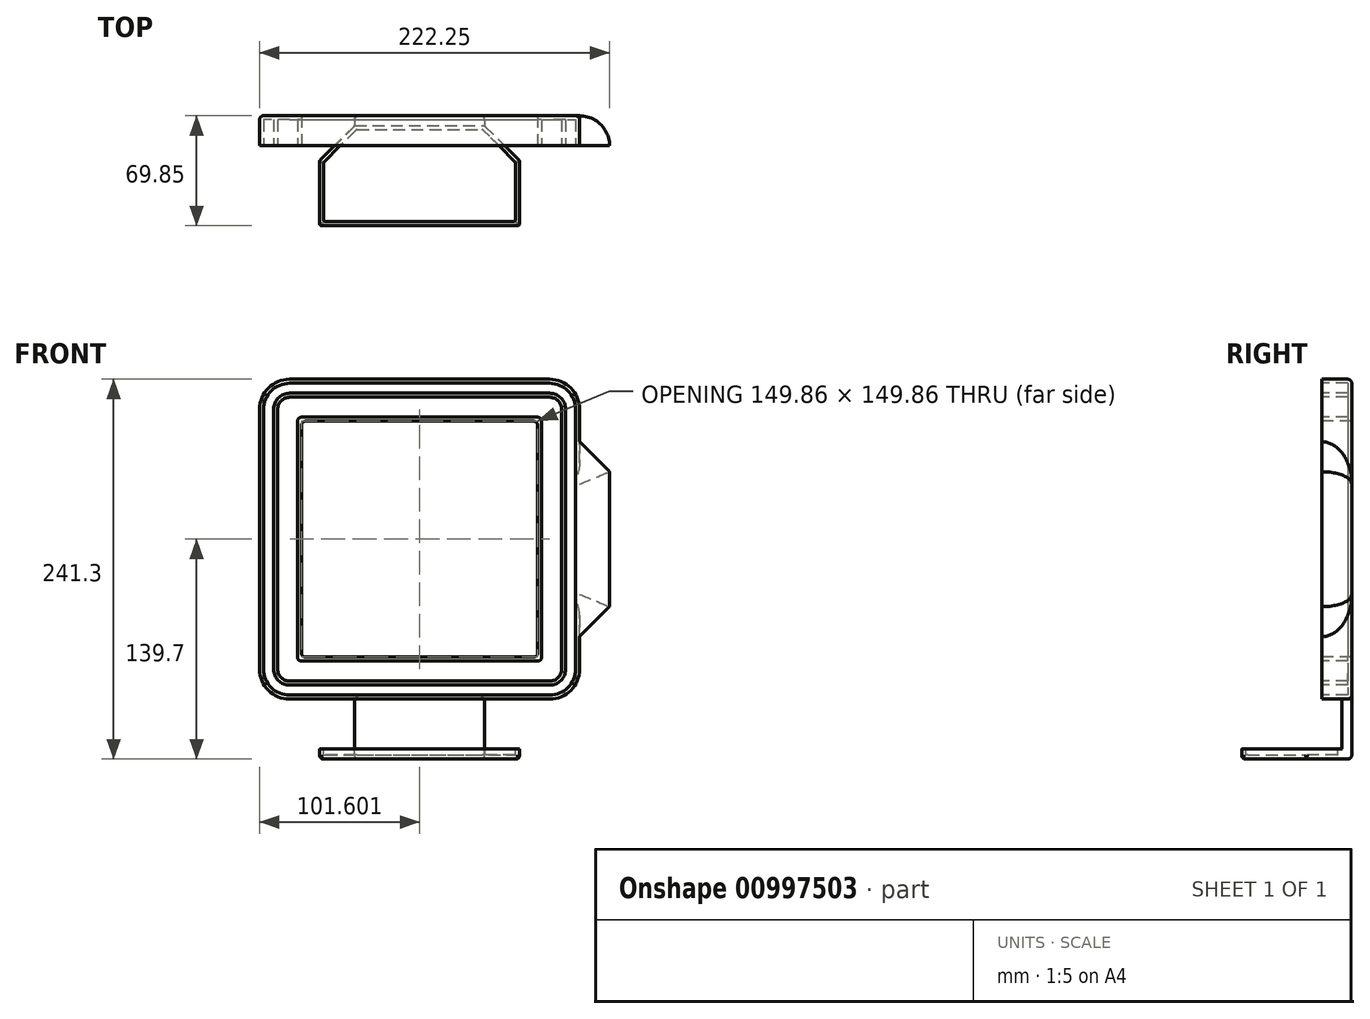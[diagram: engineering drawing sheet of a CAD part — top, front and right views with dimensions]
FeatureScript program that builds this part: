
annotation { "Feature Type Name" : "Feature", "Feature Type Description" : "" }
export const myFeature = defineFeature(function(context is Context, id is Id, definition is map)
    precondition{}
    {
        {
            var Q0;
            Q0=qCreatedBy(makeId("Front.planeOp"),FACE);
            var sketch = newSketch(context, id + "F0", { "sketchPlane" : qUnion([Q0])});
            skLineSegment(sketch, "E0.bottom", {"start": v(-101.6, 108.1) * mm, "end": v(101.6, 108.1) * mm});
            skLineSegment(sketch, "E0.top", {"start": v(-101.6, -95.1) * mm, "end": v(101.6, -95.1) * mm});
            skLineSegment(sketch, "E0.left", {"start": v(-101.6, 108.1) * mm, "end": v(-101.6, -95.1) * mm});
            skLineSegment(sketch, "E0.right", {"start": v(101.6, 108.1) * mm, "end": v(101.6, -95.1) * mm});
            skSolve(sketch);
        }
        {
            var Q0;
            Q0=makeQuery(id+"F0.imprint","IMPRINT",FACE,{"disambiguationData":[TD([[makeQuery(id+"F0.imprint","IMPRINT",EDGE,{"derivedFrom":sQuery(id+"F0.wireOp",EDGE,"E0.bottom")}),-1.0]])]});
            extrude(context, id + "F1", {"entities" : qUnion([Q0]), "depth" : 19.05 * mm, "offsetDistance" : 25.4 * mm});
        }
        {
            var Q0;
            Q0=makeQuery(id+"F1.opExtrude","SWEPT_EDGE",EDGE,{"disambiguationData":[OSD([sQuery(id+"F0.wireOp",EDGE,"E0.bottom"),sQuery(id+"F0.wireOp",EDGE,"E0.left")])]});
            var Q1;
            Q1=makeQuery(id+"F1.opExtrude","SWEPT_EDGE",EDGE,{"disambiguationData":[OSD([sQuery(id+"F0.wireOp",EDGE,"E0.top"),sQuery(id+"F0.wireOp",EDGE,"E0.left")])]});
            var Q2;
            Q2=makeQuery(id+"F1.opExtrude","SWEPT_EDGE",EDGE,{"disambiguationData":[OSD([sQuery(id+"F0.wireOp",EDGE,"E0.top"),sQuery(id+"F0.wireOp",EDGE,"E0.right")])]});
            var Q3;
            Q3=makeQuery(id+"F1.opExtrude","SWEPT_EDGE",EDGE,{"disambiguationData":[OSD([sQuery(id+"F0.wireOp",EDGE,"E0.bottom"),sQuery(id+"F0.wireOp",EDGE,"E0.right")])]});
            fillet(context, id + "F2", {"entities" : qUnion([Q0, Q1, Q2, Q3]), "tangentPropagation" : true, "radius" : 19.05 * mm, "defaultsChanged" : false, "vertexSettings" : [], "allowEdgeOverflow" : false});
        }
        {
            var Q0;
            Q0=makeQuery(id+"F1.opExtrude","CAP_FACE",FACE,{"disambiguationData":[OSD([sQuery(id+"F0.wireOp",EDGE,"E0.bottom"),sQuery(id+"F0.wireOp",EDGE,"E0.top"),sQuery(id+"F0.wireOp",EDGE,"E0.left"),sQuery(id+"F0.wireOp",EDGE,"E0.right")])],"isStart":false});
            var sketch = newSketch(context, id + "F3", { "sketchPlane" : qUnion([Q0])});
            skLineSegment(sketch, "E1.0", {"start": v(-82.55, 99.21) * mm, "end": v(82.55, 99.21) * mm});
            skArc(sketch, "E1.1", {"start": v(92.71, 89.05) * mm, "mid": v(89.74, 96.23) * mm, "end": v(82.55, 99.21) * mm});
            skArc(sketch, "E1.2", {"start": v(-82.55, 99.21) * mm, "mid": v(-89.73, 96.23) * mm, "end": v(-92.7, 89.05) * mm});
            skLineSegment(sketch, "E1.3", {"start": v(92.71, 89.05) * mm, "end": v(92.71, -76.05) * mm});
            skLineSegment(sketch, "E1.4", {"start": v(-92.7, 89.05) * mm, "end": v(-92.7, -76.05) * mm});
            skArc(sketch, "E1.5", {"start": v(-92.7, -76.05) * mm, "mid": v(-89.73, -83.23) * mm, "end": v(-82.55, -86.2) * mm});
            skLineSegment(sketch, "E1.6", {"start": v(-82.55, -86.2) * mm, "end": v(82.55, -86.2) * mm});
            skArc(sketch, "E1.7", {"start": v(82.55, -86.2) * mm, "mid": v(89.74, -83.23) * mm, "end": v(92.71, -76.05) * mm});
            skLineSegment(sketch, "E2.0", {"start": v(-74.93, 81.43) * mm, "end": v(-74.93, -68.43) * mm});
            skLineSegment(sketch, "E2.1", {"start": v(-74.93, 81.43) * mm, "end": v(74.93, 81.43) * mm});
            skLineSegment(sketch, "E2.2", {"start": v(74.93, 81.43) * mm, "end": v(74.93, -68.43) * mm});
            skLineSegment(sketch, "E2.3", {"start": v(-74.93, -68.43) * mm, "end": v(74.93, -68.43) * mm});
            skArc(sketch, "E3.0", {"start": v(-82.55, 96.67) * mm, "mid": v(-87.94, 94.44) * mm, "end": v(-90.17, 89.05) * mm});
            skLineSegment(sketch, "E3.1", {"start": v(-82.55, 96.67) * mm, "end": v(82.55, 96.67) * mm});
            skLineSegment(sketch, "E3.2", {"start": v(-90.17, 89.05) * mm, "end": v(-90.17, -76.05) * mm});
            skArc(sketch, "E3.3", {"start": v(90.17, 89.05) * mm, "mid": v(87.94, 94.44) * mm, "end": v(82.55, 96.67) * mm});
            skArc(sketch, "E3.4", {"start": v(-90.17, -76.05) * mm, "mid": v(-87.94, -81.44) * mm, "end": v(-82.55, -83.67) * mm});
            skLineSegment(sketch, "E3.5", {"start": v(-82.55, -83.67) * mm, "end": v(82.55, -83.67) * mm});
            skArc(sketch, "E3.6", {"start": v(82.55, -83.67) * mm, "mid": v(87.94, -81.44) * mm, "end": v(90.17, -76.05) * mm});
            skLineSegment(sketch, "E3.7", {"start": v(90.17, 89.05) * mm, "end": v(90.17, -76.05) * mm});
            skLineSegment(sketch, "E4.0", {"start": v(-77.47, 83.97) * mm, "end": v(-77.47, -70.97) * mm});
            skLineSegment(sketch, "E4.1", {"start": v(-77.47, 83.97) * mm, "end": v(77.47, 83.97) * mm});
            skLineSegment(sketch, "E4.2", {"start": v(77.47, 83.97) * mm, "end": v(77.47, -70.97) * mm});
            skLineSegment(sketch, "E4.3", {"start": v(-77.47, -70.97) * mm, "end": v(77.47, -70.97) * mm});
            skArc(sketch, "E5.0", {"start": v(-82.55, 105.56) * mm, "mid": v(-94.22, 100.72) * mm, "end": v(-99.06, 89.05) * mm});
            skLineSegment(sketch, "E5.1", {"start": v(-82.55, 105.56) * mm, "end": v(82.55, 105.56) * mm});
            skLineSegment(sketch, "E5.2", {"start": v(-99.06, 89.05) * mm, "end": v(-99.06, -76.05) * mm});
            skArc(sketch, "E5.3", {"start": v(99.06, 89.05) * mm, "mid": v(94.23, 100.72) * mm, "end": v(82.55, 105.56) * mm});
            skArc(sketch, "E5.4", {"start": v(-99.06, -76.05) * mm, "mid": v(-94.22, -87.72) * mm, "end": v(-82.55, -92.56) * mm});
            skLineSegment(sketch, "E5.5", {"start": v(-82.55, -92.56) * mm, "end": v(82.55, -92.56) * mm});
            skArc(sketch, "E5.6", {"start": v(82.55, -92.56) * mm, "mid": v(94.23, -87.72) * mm, "end": v(99.06, -76.05) * mm});
            skLineSegment(sketch, "E5.7", {"start": v(99.06, 89.05) * mm, "end": v(99.06, -76.05) * mm});
            skSolve(sketch);
        }
        {
            var Q0;
            Q0=makeQuery(id+"F3.imprint","IMPRINT",FACE,{"disambiguationData":[TD([[makeQuery(id+"F3.imprint","IMPRINT",EDGE,{"derivedFrom":sQuery(id+"F3.wireOp",EDGE,"E2.0")}),1.0]])]});
            extrude(context, id + "F4", {"entities" : qUnion([Q0]), "operationType" : NewBodyOperationType.REMOVE, "oppositeDirection" : true, "depth" : 25.4 * mm, "offsetDistance" : 25.4 * mm, "hasSecondDirection" : true, "secondDirectionOppositeDirection" : false, "secondDirectionDepth" : 25.4 * mm});
        }
        {
            var Q0;
            Q0=makeQuery(id+"F3.imprint","IMPRINT",FACE,{"disambiguationData":[TD([[makeQuery(id+"F3.imprint","IMPRINT",EDGE,{"derivedFrom":sQuery(id+"F3.wireOp",EDGE,"E3.0")}),1.0]])]});
            var Q1;
            Q1=makeQuery(id+"F3.imprint","IMPRINT",FACE,{"disambiguationData":[TD([[makeQuery(id+"F3.imprint","IMPRINT",EDGE,{"derivedFrom":sQuery(id+"F3.wireOp",EDGE,"E1.0")}),1.0]])]});
            extrude(context, id + "F5", {"entities" : qUnion([Q0, Q1]), "operationType" : NewBodyOperationType.REMOVE, "oppositeDirection" : true, "depth" : 16.5 * mm, "offsetDistance" : 25.4 * mm});
        }
        {
            var Q0;
            Q0=makeQuery(id+"F4.boolean.opBoolean","COPY",EDGE,{"derivedFrom":makeQuery(id+"F4.opExtrude","SWEPT_EDGE",EDGE,{"disambiguationData":[OSD([sQuery(id+"F3.wireOp",EDGE,"E2.1"),sQuery(id+"F3.wireOp",EDGE,"E2.2")])]})});
            var Q1;
            Q1=makeQuery(id+"F5.boolean.opBoolean","COPY",EDGE,{"derivedFrom":makeQuery(id+"F5.opExtrude","SWEPT_EDGE",EDGE,{"disambiguationData":[OSD([sQuery(id+"F3.wireOp",EDGE,"E4.1"),sQuery(id+"F3.wireOp",EDGE,"E4.2")])]})});
            var Q2;
            Q2=makeQuery(id+"F4.boolean.opBoolean","COPY",EDGE,{"derivedFrom":makeQuery(id+"F4.opExtrude","SWEPT_EDGE",EDGE,{"disambiguationData":[OSD([sQuery(id+"F3.wireOp",EDGE,"E2.2"),sQuery(id+"F3.wireOp",EDGE,"E2.3")])]})});
            var Q3;
            Q3=makeQuery(id+"F5.boolean.opBoolean","COPY",EDGE,{"derivedFrom":makeQuery(id+"F5.opExtrude","SWEPT_EDGE",EDGE,{"disambiguationData":[OSD([sQuery(id+"F3.wireOp",EDGE,"E4.2"),sQuery(id+"F3.wireOp",EDGE,"E4.3")])]})});
            var Q4;
            Q4=makeQuery(id+"F5.boolean.opBoolean","COPY",EDGE,{"derivedFrom":makeQuery(id+"F5.opExtrude","SWEPT_EDGE",EDGE,{"disambiguationData":[OSD([sQuery(id+"F3.wireOp",EDGE,"E4.0"),sQuery(id+"F3.wireOp",EDGE,"E4.3")])]})});
            var Q5;
            Q5=makeQuery(id+"F4.boolean.opBoolean","COPY",EDGE,{"derivedFrom":makeQuery(id+"F4.opExtrude","SWEPT_EDGE",EDGE,{"disambiguationData":[OSD([sQuery(id+"F3.wireOp",EDGE,"E2.0"),sQuery(id+"F3.wireOp",EDGE,"E2.3")])]})});
            var Q6;
            Q6=makeQuery(id+"F4.boolean.opBoolean","COPY",EDGE,{"derivedFrom":makeQuery(id+"F4.opExtrude","SWEPT_EDGE",EDGE,{"disambiguationData":[OSD([sQuery(id+"F3.wireOp",EDGE,"E2.0"),sQuery(id+"F3.wireOp",EDGE,"E2.1")])]})});
            var Q7;
            Q7=makeQuery(id+"F5.boolean.opBoolean","COPY",EDGE,{"derivedFrom":makeQuery(id+"F5.opExtrude","SWEPT_EDGE",EDGE,{"disambiguationData":[OSD([sQuery(id+"F3.wireOp",EDGE,"E4.0"),sQuery(id+"F3.wireOp",EDGE,"E4.1")])]})});
            fillet(context, id + "F6", {"entities" : qUnion([Q0, Q1, Q2, Q3, Q4, Q5, Q6, Q7]), "tangentPropagation" : true, "radius" : 2.54 * mm, "defaultsChanged" : true, "vertexSettings" : [], "allowEdgeOverflow" : false});
        }
        {
            var Q0;
            {var subQ0=sQuery(id+"F0.wireOp",EDGE,"E0.right");var subQ1=sQuery(id+"F0.wireOp",EDGE,"E0.top");var subQ2=sQuery(id+"F0.wireOp",EDGE,"E0.left");var subQ3=sQuery(id+"F0.wireOp",EDGE,"E0.bottom");Q0=makeQuery(id+"F5.boolean.opBoolean","SPLIT",FACE,{"disambiguationData":[TD([makeQuery(id+"F1.opExtrude","SWEPT_FACE",FACE,{"disambiguationData":[OSD([subQ3])]})])],"derivedFrom":makeQuery(id+"F1.opExtrude","CAP_FACE",FACE,{"disambiguationData":[OSD([subQ3,subQ1,subQ2,subQ0])],"isStart":false})});}
            var sketch = newSketch(context, id + "F7", { "sketchPlane" : qUnion([Q0])});
            skPoint(sketch, "E6", {"position": v(0, -95.1) * mm});
            skPoint(sketch, "E7", {"position": v(-41.27, -95.1) * mm});
            skPoint(sketch, "E8", {"position": v(41.28, -95.1) * mm});
            skPoint(sketch, "E9", {"position": v(82.55, -95.1) * mm});
            skPoint(sketch, "E10", {"position": v(-82.55, -95.1) * mm});
            skPoint(sketch, "E11", {"position": v(101.6, 89.05) * mm});
            skPoint(sketch, "E12", {"position": v(101.6, 6.5) * mm});
            skPoint(sketch, "E13", {"position": v(101.6, -76.05) * mm});
            skPoint(sketch, "E14", {"position": v(101.6, -34.77) * mm});
            skPoint(sketch, "E15", {"position": v(101.6, 47.78) * mm});
            skPoint(sketch, "E16", {"position": v(101.6, 68.41) * mm});
            skPoint(sketch, "E17", {"position": v(101.6, -55.41) * mm});
            skLineSegment(sketch, "E18.bottom", {"start": v(101.6, 68.41) * mm, "end": v(120.65, 68.41) * mm});
            skLineSegment(sketch, "E18.top", {"start": v(101.6, -55.41) * mm, "end": v(120.65, -55.41) * mm});
            skLineSegment(sketch, "E18.left", {"start": v(101.6, 68.41) * mm, "end": v(101.6, -55.41) * mm});
            skLineSegment(sketch, "E18.right", {"start": v(120.65, 68.41) * mm, "end": v(120.65, -55.41) * mm});
            skSolve(sketch);
        }
        {
            var Q0;
            Q0=makeQuery(id+"F7.imprint","IMPRINT",FACE,{"disambiguationData":[TD([[makeQuery(id+"F7.imprint","IMPRINT",EDGE,{"derivedFrom":sQuery(id+"F7.wireOp",EDGE,"E18.bottom")}),-1.0]])]});
            extrude(context, id + "F8", {"entities" : qUnion([Q0]), "operationType" : NewBodyOperationType.ADD, "oppositeDirection" : true, "depth" : 19.05 * mm, "offsetDistance" : 25.4 * mm});
        }
        {
            var Q0;
            Q0=makeQuery(id+"F8.opExtrude","SWEPT_EDGE",EDGE,{"disambiguationData":[OSD([sQuery(id+"F7.wireOp",EDGE,"E18.top"),sQuery(id+"F7.wireOp",EDGE,"E18.right")])]});
            var Q1;
            Q1=makeQuery(id+"F8.opExtrude","SWEPT_EDGE",EDGE,{"disambiguationData":[OSD([sQuery(id+"F7.wireOp",EDGE,"E18.bottom"),sQuery(id+"F7.wireOp",EDGE,"E18.right")])]});
            chamfer(context, id + "F9", {"entities" : qUnion([Q0, Q1]), "width" : 19.05 * mm, "tangentPropagation" : true});
        }
        {
            var Q0;
            Q0=makeQuery(id+"F8.opExtrude","CAP_EDGE",EDGE,{"disambiguationData":[OSD([sQuery(id+"F7.wireOp",EDGE,"E18.right")])],"isStart":false});
            var Q1;
            {var subQ0=sQuery(id+"F7.wireOp",EDGE,"E18.right");var subQ1=sQuery(id+"F7.wireOp",EDGE,"E18.top");Q1=makeQuery(id+"F9.opChamfer","BLEND_EDGE",EDGE,{"blendedFrom":[makeQuery(id+"F8.opExtrude","SWEPT_EDGE",EDGE,{"disambiguationData":[OSD([subQ1,subQ0])]}),makeQuery(id+"F8.boolean.opBoolean","MERGE",FACE,{"derivedFrom":[makeQuery(id+"F1.opExtrude","CAP_FACE",FACE,{"disambiguationData":[OSD([sQuery(id+"F0.wireOp",EDGE,"E0.bottom"),sQuery(id+"F0.wireOp",EDGE,"E0.top"),sQuery(id+"F0.wireOp",EDGE,"E0.left"),sQuery(id+"F0.wireOp",EDGE,"E0.right")])],"isStart":true}),makeQuery(id+"F8.opExtrude","CAP_FACE",FACE,{"disambiguationData":[OSD([sQuery(id+"F7.wireOp",EDGE,"E18.bottom"),subQ1,sQuery(id+"F7.wireOp",EDGE,"E18.left"),subQ0])],"isStart":false})]})],"blendedInto":[makeQuery(id+"F8.boolean.opBoolean","MERGE",FACE,{"derivedFrom":[makeQuery(id+"F1.opExtrude","CAP_FACE",FACE,{"disambiguationData":[OSD([sQuery(id+"F0.wireOp",EDGE,"E0.bottom"),sQuery(id+"F0.wireOp",EDGE,"E0.top"),sQuery(id+"F0.wireOp",EDGE,"E0.left"),sQuery(id+"F0.wireOp",EDGE,"E0.right")])],"isStart":true}),makeQuery(id+"F8.opExtrude","CAP_FACE",FACE,{"disambiguationData":[OSD([sQuery(id+"F7.wireOp",EDGE,"E18.bottom"),subQ1,sQuery(id+"F7.wireOp",EDGE,"E18.left"),subQ0])],"isStart":false})]})]});}
            var Q2;
            {var subQ0=sQuery(id+"F7.wireOp",EDGE,"E18.right");var subQ1=sQuery(id+"F7.wireOp",EDGE,"E18.bottom");Q2=makeQuery(id+"F9.opChamfer","BLEND_EDGE",EDGE,{"blendedFrom":[makeQuery(id+"F8.opExtrude","SWEPT_EDGE",EDGE,{"disambiguationData":[OSD([subQ1,subQ0])]}),makeQuery(id+"F8.boolean.opBoolean","MERGE",FACE,{"derivedFrom":[makeQuery(id+"F1.opExtrude","CAP_FACE",FACE,{"disambiguationData":[OSD([sQuery(id+"F0.wireOp",EDGE,"E0.bottom"),sQuery(id+"F0.wireOp",EDGE,"E0.top"),sQuery(id+"F0.wireOp",EDGE,"E0.left"),sQuery(id+"F0.wireOp",EDGE,"E0.right")])],"isStart":true}),makeQuery(id+"F8.opExtrude","CAP_FACE",FACE,{"disambiguationData":[OSD([subQ1,sQuery(id+"F7.wireOp",EDGE,"E18.top"),sQuery(id+"F7.wireOp",EDGE,"E18.left"),subQ0])],"isStart":false})]})],"blendedInto":[makeQuery(id+"F8.boolean.opBoolean","MERGE",FACE,{"derivedFrom":[makeQuery(id+"F1.opExtrude","CAP_FACE",FACE,{"disambiguationData":[OSD([sQuery(id+"F0.wireOp",EDGE,"E0.bottom"),sQuery(id+"F0.wireOp",EDGE,"E0.top"),sQuery(id+"F0.wireOp",EDGE,"E0.left"),sQuery(id+"F0.wireOp",EDGE,"E0.right")])],"isStart":true}),makeQuery(id+"F8.opExtrude","CAP_FACE",FACE,{"disambiguationData":[OSD([subQ1,sQuery(id+"F7.wireOp",EDGE,"E18.top"),sQuery(id+"F7.wireOp",EDGE,"E18.left"),subQ0])],"isStart":false})]})]});}
            fillet(context, id + "F10", {"entities" : qUnion([Q0, Q1, Q2]), "tangentPropagation" : true, "radius" : 19.05 * mm, "defaultsChanged" : false, "vertexSettings" : [], "allowEdgeOverflow" : false});
        }
        {
            var Q0;
            Q0=makeQuery(id+"F1.opExtrude","SWEPT_FACE",FACE,{"disambiguationData":[OSD([sQuery(id+"F0.wireOp",EDGE,"E0.top")])]});
            var sketch = newSketch(context, id + "F11", { "sketchPlane" : qUnion([Q0])});
            skPoint(sketch, "E19", {"position": v(-82.55, 0) * mm});
            skPoint(sketch, "E20", {"position": v(0, 0) * mm});
            skPoint(sketch, "E21", {"position": v(82.55, 0) * mm});
            skPoint(sketch, "E22", {"position": v(41.28, 0) * mm});
            skPoint(sketch, "E23", {"position": v(-41.27, 0) * mm});
            skLineSegment(sketch, "E24.bottom", {"start": v(-41.27, 0) * mm, "end": v(41.28, 0) * mm});
            skLineSegment(sketch, "E24.top", {"start": v(-41.27, 6.35) * mm, "end": v(41.28, 6.35) * mm});
            skLineSegment(sketch, "E24.left", {"start": v(-41.27, 0) * mm, "end": v(-41.27, 6.35) * mm});
            skLineSegment(sketch, "E24.right", {"start": v(41.28, 0) * mm, "end": v(41.28, 6.35) * mm});
            skSolve(sketch);
        }
        {
            var Q0;
            Q0=makeQuery(id+"F11.imprint","IMPRINT",FACE,{"disambiguationData":[TD([[makeQuery(id+"F11.imprint","IMPRINT",EDGE,{"derivedFrom":sQuery(id+"F11.wireOp",EDGE,"E24.bottom")}),1.0]])]});
            extrude(context, id + "F12", {"entities" : qUnion([Q0]), "operationType" : NewBodyOperationType.ADD, "depth" : 38.1 * mm, "offsetDistance" : 25.4 * mm});
        }
        {
            var Q0;
            Q0=makeQuery(id+"F12.opExtrude","SWEPT_FACE",FACE,{"disambiguationData":[OSD([sQuery(id+"F11.wireOp",EDGE,"E24.top")])]});
            var sketch = newSketch(context, id + "F13", { "sketchPlane" : qUnion([Q0])});
            skLineSegment(sketch, "E25.bottom", {"start": v(-63.5, -133.2) * mm, "end": v(63.5, -133.2) * mm});
            skLineSegment(sketch, "E25.top", {"start": v(-63.5, -126.85) * mm, "end": v(63.5, -126.85) * mm});
            skLineSegment(sketch, "E25.left", {"start": v(-63.5, -133.2) * mm, "end": v(-63.5, -126.85) * mm});
            skLineSegment(sketch, "E25.right", {"start": v(63.5, -133.2) * mm, "end": v(63.5, -126.85) * mm});
            skSolve(sketch);
        }
        {
            var Q0;
            {var subQ3=sQuery(id+"F13.wireOp",EDGE,"E25.left");Q0=makeQuery(id+"F13.imprint","IMPRINT",FACE,{"disambiguationData":[TD([[makeQuery(id+"F13.imprint","IMPRINT",EDGE,{"derivedFrom":subQ3}),-1.0]])]});}
            var Q1;
            {var subQ0=sQuery(id+"F13.wireOp",EDGE,"E25.bottom");var subQ1=sQuery(id+"F11.wireOp",EDGE,"E24.top");var subQ2=makeQuery(id+"F12.opExtrude","SWEPT_EDGE",EDGE,{"disambiguationData":[OSD([subQ1,sQuery(id+"F11.wireOp",EDGE,"E24.left")])]});var subQ3=makeQuery(id+"F13.imprint","INTERSECT",VERTEX,{"derivedFrom":[subQ2,subQ0]});Q1=makeQuery(id+"F13.imprint","IMPRINT",FACE,{"disambiguationData":[TD([[makeQuery(id+"F13.imprint","IMPRINT",EDGE,{"disambiguationData":[TD([[subQ3,-1.0]])],"derivedFrom":subQ0}),1.0]])]});}
            var Q2;
            {var subQ3=sQuery(id+"F13.wireOp",EDGE,"E25.right");Q2=makeQuery(id+"F13.imprint","IMPRINT",FACE,{"disambiguationData":[TD([[makeQuery(id+"F13.imprint","IMPRINT",EDGE,{"derivedFrom":subQ3}),1.0]])]});}
            extrude(context, id + "F14", {"entities" : qUnion([Q0, Q1, Q2]), "operationType" : NewBodyOperationType.ADD, "depth" : 63.5 * mm, "offsetDistance" : 25.4 * mm});
        }
        {
            var Q0;
            Q0=makeQuery(id+"F14.opExtrude","CAP_EDGE",EDGE,{"disambiguationData":[OSD([sQuery(id+"F13.wireOp",EDGE,"E25.left")])],"isStart":true});
            var Q1;
            Q1=makeQuery(id+"F14.opExtrude","CAP_EDGE",EDGE,{"disambiguationData":[OSD([sQuery(id+"F13.wireOp",EDGE,"E25.right")])],"isStart":true});
            chamfer(context, id + "F15", {"entities" : qUnion([Q0, Q1]), "width" : 22.22 * mm, "tangentPropagation" : true});
        }
        {
            var Q0;
            Q0=makeQuery(id+"F14.opExtrude","SWEPT_FACE",FACE,{"disambiguationData":[OSD([sQuery(id+"F13.wireOp",EDGE,"E25.top")])]});
            var sketch = newSketch(context, id + "F16", { "sketchPlane" : qUnion([Q0])});
            skLineSegment(sketch, "E26.0", {"start": v(-40.22, -8.9) * mm, "end": v(40.22, -8.9) * mm});
            skLineSegment(sketch, "E26.1", {"start": v(-60.96, -67.3) * mm, "end": v(-60.96, -29.63) * mm});
            skLineSegment(sketch, "E26.2", {"start": v(-60.96, -67.3) * mm, "end": v(60.96, -67.3) * mm});
            skLineSegment(sketch, "E26.3", {"start": v(-40.22, -8.9) * mm, "end": v(-60.96, -29.63) * mm});
            skLineSegment(sketch, "E26.4", {"start": v(60.96, -67.3) * mm, "end": v(60.96, -29.63) * mm});
            skLineSegment(sketch, "E26.5", {"start": v(60.96, -29.63) * mm, "end": v(40.22, -8.9) * mm});
            skSolve(sketch);
        }
        {
            var Q0;
            Q0=makeQuery(id+"F16.imprint","IMPRINT",FACE,{"disambiguationData":[TD([[makeQuery(id+"F16.imprint","IMPRINT",EDGE,{"derivedFrom":sQuery(id+"F16.wireOp",EDGE,"E26.0")}),-1.0]])]});
            extrude(context, id + "F17", {"entities" : qUnion([Q0]), "operationType" : NewBodyOperationType.REMOVE, "oppositeDirection" : true, "depth" : 3.8 * mm, "offsetDistance" : 25.4 * mm});
        }
        {
            var Q0;
            Q0=makeQuery(id+"F14.opExtrude","CAP_EDGE",EDGE,{"disambiguationData":[OSD([sQuery(id+"F13.wireOp",EDGE,"E25.left")])],"isStart":false});
            var Q1;
            Q1=makeQuery(id+"F14.opExtrude","CAP_EDGE",EDGE,{"disambiguationData":[OSD([sQuery(id+"F13.wireOp",EDGE,"E25.right")])],"isStart":false});
            var Q2;
            {var subQ0=sQuery(id+"F13.wireOp",EDGE,"E25.right");Q2=makeQuery(id+"F15.opChamfer","BLEND_EDGE",EDGE,{"blendedFrom":[makeQuery(id+"F14.opExtrude","CAP_EDGE",EDGE,{"disambiguationData":[OSD([subQ0])],"isStart":true}),makeQuery(id+"F14.opExtrude","SWEPT_FACE",FACE,{"disambiguationData":[OSD([subQ0])]})],"blendedInto":[makeQuery(id+"F14.opExtrude","SWEPT_FACE",FACE,{"disambiguationData":[OSD([subQ0])]})]});}
            var Q3;
            Q3=makeQuery(id+"F15.opChamfer","BLEND_EDGE",EDGE,{"blendedFrom":[makeQuery(id+"F14.opExtrude","CAP_EDGE",EDGE,{"disambiguationData":[OSD([sQuery(id+"F13.wireOp",EDGE,"E25.right")])],"isStart":true}),makeQuery(id+"F12.opExtrude","SWEPT_FACE",FACE,{"disambiguationData":[OSD([sQuery(id+"F11.wireOp",EDGE,"E24.right")])]})],"blendedInto":[makeQuery(id+"F12.opExtrude","SWEPT_FACE",FACE,{"disambiguationData":[OSD([sQuery(id+"F11.wireOp",EDGE,"E24.right")])]})]});
            var Q4;
            Q4=makeQuery(id+"F17.boolean.opBoolean","COPY",EDGE,{"derivedFrom":makeQuery(id+"F17.opExtrude","SWEPT_EDGE",EDGE,{"disambiguationData":[OSD([sQuery(id+"F16.wireOp",EDGE,"E26.0"),sQuery(id+"F16.wireOp",EDGE,"E26.5")])]})});
            var Q5;
            Q5=makeQuery(id+"F17.boolean.opBoolean","COPY",EDGE,{"derivedFrom":makeQuery(id+"F17.opExtrude","SWEPT_EDGE",EDGE,{"disambiguationData":[OSD([sQuery(id+"F16.wireOp",EDGE,"E26.1"),sQuery(id+"F16.wireOp",EDGE,"E26.3")])]})});
            var Q6;
            {var subQ0=sQuery(id+"F13.wireOp",EDGE,"E25.left");Q6=makeQuery(id+"F15.opChamfer","BLEND_EDGE",EDGE,{"blendedFrom":[makeQuery(id+"F14.opExtrude","CAP_EDGE",EDGE,{"disambiguationData":[OSD([subQ0])],"isStart":true}),makeQuery(id+"F14.opExtrude","SWEPT_FACE",FACE,{"disambiguationData":[OSD([subQ0])]})],"blendedInto":[makeQuery(id+"F14.opExtrude","SWEPT_FACE",FACE,{"disambiguationData":[OSD([subQ0])]})]});}
            var Q7;
            Q7=makeQuery(id+"F17.boolean.opBoolean","COPY",EDGE,{"derivedFrom":makeQuery(id+"F17.opExtrude","SWEPT_EDGE",EDGE,{"disambiguationData":[OSD([sQuery(id+"F16.wireOp",EDGE,"E26.0"),sQuery(id+"F16.wireOp",EDGE,"E26.3")])]})});
            var Q8;
            Q8=makeQuery(id+"F15.opChamfer","BLEND_EDGE",EDGE,{"blendedFrom":[makeQuery(id+"F14.opExtrude","CAP_EDGE",EDGE,{"disambiguationData":[OSD([sQuery(id+"F13.wireOp",EDGE,"E25.left")])],"isStart":true}),makeQuery(id+"F12.opExtrude","SWEPT_FACE",FACE,{"disambiguationData":[OSD([sQuery(id+"F11.wireOp",EDGE,"E24.left")])]})],"blendedInto":[makeQuery(id+"F12.opExtrude","SWEPT_FACE",FACE,{"disambiguationData":[OSD([sQuery(id+"F11.wireOp",EDGE,"E24.left")])]})]});
            var Q9;
            Q9=makeQuery(id+"F17.boolean.opBoolean","COPY",EDGE,{"derivedFrom":makeQuery(id+"F17.opExtrude","SWEPT_EDGE",EDGE,{"disambiguationData":[OSD([sQuery(id+"F16.wireOp",EDGE,"E26.1"),sQuery(id+"F16.wireOp",EDGE,"E26.2")])]})});
            var Q10;
            Q10=makeQuery(id+"F17.boolean.opBoolean","COPY",EDGE,{"derivedFrom":makeQuery(id+"F17.opExtrude","SWEPT_EDGE",EDGE,{"disambiguationData":[OSD([sQuery(id+"F16.wireOp",EDGE,"E26.2"),sQuery(id+"F16.wireOp",EDGE,"E26.4")])]})});
            var Q11;
            Q11=makeQuery(id+"F17.boolean.opBoolean","COPY",EDGE,{"derivedFrom":makeQuery(id+"F17.opExtrude","SWEPT_EDGE",EDGE,{"disambiguationData":[OSD([sQuery(id+"F16.wireOp",EDGE,"E26.4"),sQuery(id+"F16.wireOp",EDGE,"E26.5")])]})});
            var Q12;
            {var subQ0=sQuery(id+"F13.wireOp",EDGE,"E25.top");Q12=makeQuery(id+"F14.boolean.opBoolean","SPLIT",EDGE,{"disambiguationData":[topologyDisambiguationEdgeConnected([makeQuery(id+"F12.opExtrude","SWEPT_FACE",FACE,{"disambiguationData":[OSD([sQuery(id+"F11.wireOp",EDGE,"E24.top")])]}),makeQuery(id+"F14.opExtrude","SWEPT_FACE",FACE,{"disambiguationData":[OSD([subQ0])]})])],"derivedFrom":makeQuery(id+"F14.opExtrude","CAP_EDGE",EDGE,{"disambiguationData":[OSD([subQ0])],"isStart":true})});}
            fillet(context, id + "F18", {"entities" : qUnion([Q0, Q1, Q2, Q3, Q4, Q5, Q6, Q7, Q8, Q9, Q10, Q11, Q12]), "tangentPropagation" : true, "radius" : 1.27 * mm, "defaultsChanged" : false, "vertexSettings" : [], "allowEdgeOverflow" : false});
        }
        {
            var Q0;
            Q0=makeQuery(id+"F1.opExtrude","CAP_EDGE",EDGE,{"disambiguationData":[OSD([sQuery(id+"F0.wireOp",EDGE,"E0.left")])],"isStart":true});
            var Q1;
            Q1=makeQuery(id+"F12.opExtrude","SWEPT_EDGE",EDGE,{"disambiguationData":[OSD([sQuery(id+"F0.wireOp",EDGE,"E0.top"),sQuery(id+"F11.wireOp",EDGE,"E24.bottom"),sQuery(id+"F11.wireOp",EDGE,"E24.left")])]});
            var Q2;
            Q2=makeQuery(id+"F12.opExtrude","CAP_EDGE",EDGE,{"disambiguationData":[OSD([sQuery(id+"F11.wireOp",EDGE,"E24.bottom")])],"isStart":false});
            var Q3;
            Q3=makeQuery(id+"F12.opExtrude","SWEPT_EDGE",EDGE,{"disambiguationData":[OSD([sQuery(id+"F0.wireOp",EDGE,"E0.top"),sQuery(id+"F11.wireOp",EDGE,"E24.bottom"),sQuery(id+"F11.wireOp",EDGE,"E24.right")])]});
            var Q4;
            {var subQ1=sQuery(id+"F0.wireOp",EDGE,"E0.top");Q4=makeQuery(id+"F12.boolean.opBoolean","SPLIT",EDGE,{"disambiguationData":[TD([makeQuery(id+"F12.opExtrude","SWEPT_FACE",FACE,{"disambiguationData":[OSD([sQuery(id+"F11.wireOp",EDGE,"E24.right")])]})])],"derivedFrom":makeQuery(id+"F1.opExtrude","CAP_EDGE",EDGE,{"disambiguationData":[OSD([subQ1])],"isStart":true})});}
            var Q5;
            Q5=makeQuery(id+"F14.opExtrude","SWEPT_EDGE",EDGE,{"disambiguationData":[OSD([sQuery(id+"F13.wireOp",EDGE,"E25.bottom"),sQuery(id+"F13.wireOp",EDGE,"E25.left")])]});
            fillet(context, id + "F19", {"entities" : qUnion([Q0, Q1, Q2, Q3, Q4, Q5]), "tangentPropagation" : true, "radius" : 2.54 * mm, "defaultsChanged" : false, "vertexSettings" : [], "allowEdgeOverflow" : false});
        }
    });
